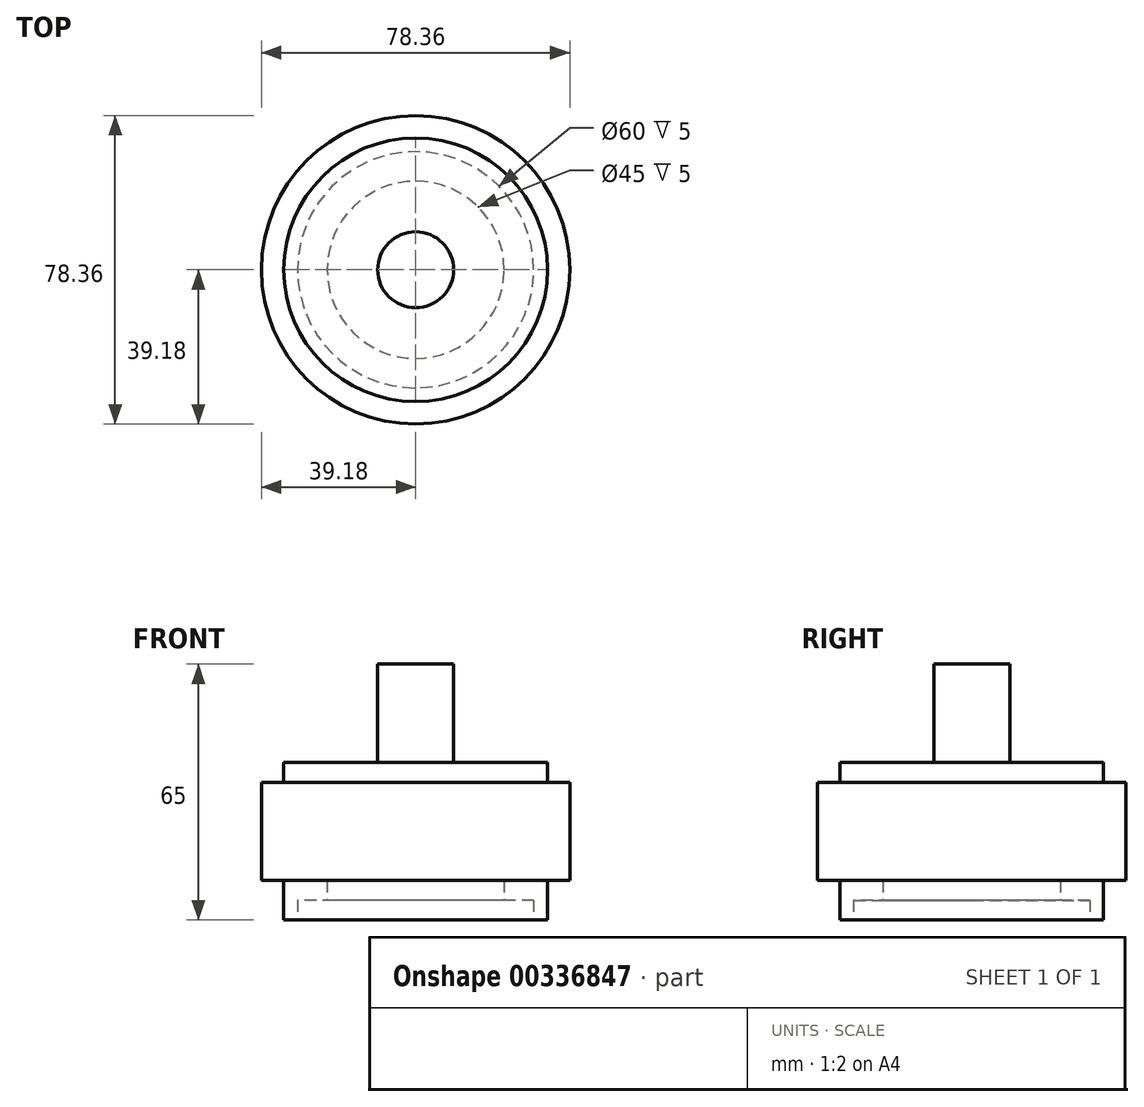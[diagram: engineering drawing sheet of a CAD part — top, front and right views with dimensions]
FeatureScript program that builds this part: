
annotation { "Feature Type Name" : "Feature", "Feature Type Description" : "" }
export const myFeature = defineFeature(function(context is Context, id is Id, definition is map)
    precondition{}
    {
        {
            var Q0;
            Q0=qCreatedBy(makeId("Top.planeOp"),FACE);
            var sketch = newSketch(context, id + "F0", { "sketchPlane" : qUnion([Q0])});
            skCircle(sketch, "E0", {"center": v(0, 0) * mm, "radius": 30 * mm});
            skCircle(sketch, "E1", {"center": v(0, 0) * mm, "radius": 33.5 * mm});
            skSolve(sketch);
        }
        {
            var Q0;
            Q0=makeQuery(id+"F0.imprint","IMPRINT",FACE,{"disambiguationData":[TD([[makeQuery(id+"F0.imprint","IMPRINT",EDGE,{"derivedFrom":sQuery(id+"F0.wireOp",EDGE,"E0")}),-1.0]])]});
            var Q1;
            Q1=makeQuery(id+"F0.imprint","IMPRINT",FACE,{"disambiguationData":[TD([[makeQuery(id+"F0.imprint","IMPRINT",EDGE,{"derivedFrom":sQuery(id+"F0.wireOp",EDGE,"E0")}),1.0]])]});
            extrude(context, id + "F1", {"entities" : qUnion([Q0, Q1]), "depth" : 40 * mm});
        }
        {
            var Q0;
            Q0=makeQuery(id+"F0.imprint","IMPRINT",FACE,{"disambiguationData":[TD([[makeQuery(id+"F0.imprint","IMPRINT",EDGE,{"derivedFrom":sQuery(id+"F0.wireOp",EDGE,"E0")}),1.0]])]});
            extrude(context, id + "F2", {"entities" : qUnion([Q0]), "operationType" : NewBodyOperationType.REMOVE, "depth" : 5 * mm});
        }
        {
            var Q0;
            Q0=makeQuery(id+"F1.opExtrude","CAP_FACE",FACE,{"disambiguationData":[OSD([sQuery(id+"F0.wireOp",EDGE,"E1")])],"isStart":false});
            var sketch = newSketch(context, id + "F3", { "sketchPlane" : qUnion([Q0])});
            skCircle(sketch, "E2", {"center": v(0, 0) * mm, "radius": 20.5 * mm});
            skSolve(sketch);
        }
        {
            var Q0;
            Q0=makeQuery(id+"F0.imprint","IMPRINT",FACE,{"disambiguationData":[TD([[makeQuery(id+"F0.imprint","IMPRINT",EDGE,{"derivedFrom":sQuery(id+"F0.wireOp",EDGE,"E0")}),1.0]])]});
            var sketch = newSketch(context, id + "F4", { "sketchPlane" : qUnion([Q0])});
            skCircle(sketch, "E3", {"center": v(0, 0) * mm, "radius": 22.5 * mm});
            skSolve(sketch);
        }
        {
            var Q0;
            Q0=makeQuery(id+"F4.imprint","IMPRINT",FACE,{"disambiguationData":[TD([[makeQuery(id+"F4.imprint","IMPRINT",EDGE,{"derivedFrom":sQuery(id+"F4.wireOp",EDGE,"E3")}),1.0]])]});
            extrude(context, id + "F5", {"entities" : qUnion([Q0]), "operationType" : NewBodyOperationType.REMOVE, "depth" : 15 * mm});
        }
        {
            var Q0;
            Q0=makeQuery(id+"F3.imprint","IMPRINT",FACE,{"disambiguationData":[TD([[makeQuery(id+"F3.imprint","IMPRINT",EDGE,{"derivedFrom":sQuery(id+"F3.wireOp",EDGE,"E2")}),1.0]])]});
            var sketch = newSketch(context, id + "F6", { "sketchPlane" : qUnion([Q0])});
            skCircle(sketch, "E4", {"center": v(0, 0) * mm, "radius": 9.65 * mm});
            skSolve(sketch);
        }
        {
            var Q0;
            Q0 = qSketchRegion(id + "F6", true);
            extrude(context, id + "F7", {"entities" : qUnion([Q0]), "operationType" : NewBodyOperationType.ADD, "depth" : 25 * mm});
        }
        {
            var Q0;
            Q0=qCreatedBy(makeId("Top.planeOp"),FACE);
            cPlane(context, id + "F8", {"entities" : qUnion([Q0]), "cplaneType" : CPlaneType.OFFSET, "offset" : 10 * mm, "width" : 150 * mm, "height" : 150 * mm});
        }
        {
            var Q0;
            Q0=qCreatedBy(id+"F8.planeOp",FACE);
            var sketch = newSketch(context, id + "F9", { "sketchPlane" : qUnion([Q0])});
            skCircle(sketch, "E5", {"center": v(0, 0) * mm, "radius": 39.18 * mm});
            skSolve(sketch);
        }
        {
            var Q0;
            Q0 = qSketchRegion(id + "F9", true);
            extrude(context, id + "F10", {"entities" : qUnion([Q0]), "operationType" : NewBodyOperationType.ADD, "depth" : 25 * mm});
        }
    });
